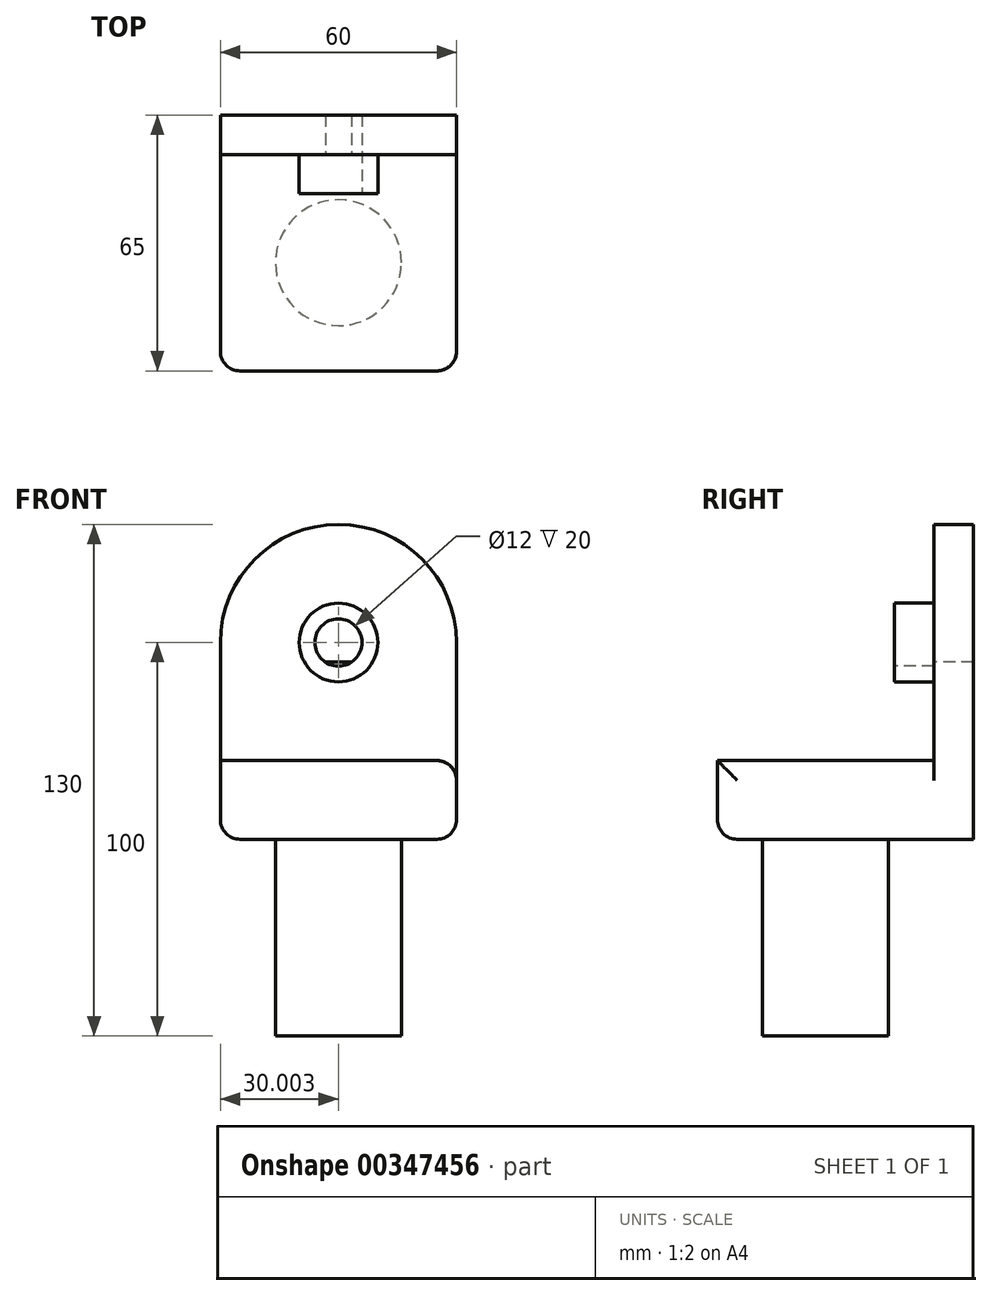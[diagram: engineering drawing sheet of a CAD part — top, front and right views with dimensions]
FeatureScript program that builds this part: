
annotation { "Feature Type Name" : "Feature", "Feature Type Description" : "" }
export const myFeature = defineFeature(function(context is Context, id is Id, definition is map)
    precondition{}
    {
        {
            var Q0;
            Q0=qCreatedBy(makeId("Top.planeOp"),FACE);
            var sketch = newSketch(context, id + "F0", { "sketchPlane" : qUnion([Q0])});
            skCircle(sketch, "E0", {"center": v(-36.32, -31.14) * mm, "radius": 16 * mm});
            skSolve(sketch);
        }
        {
            var Q0;
            Q0 = qSketchRegion(id + "F0", true);
            extrude(context, id + "F1", {"entities" : qUnion([Q0]), "depth" : 50 * mm});
        }
        {
            var Q0;
            Q0=makeQuery(id+"F1.opExtrude","CAP_FACE",FACE,{"disambiguationData":[OSD([sQuery(id+"F0.wireOp",EDGE,"E0")])],"isStart":false});
            var sketch = newSketch(context, id + "F2", { "sketchPlane" : qUnion([Q0])});
            skLineSegment(sketch, "E1", {"start": v(-66.32, -31.14) * mm, "end": v(-66.32, -3.64) * mm});
            skLineSegment(sketch, "E2", {"start": v(-66.32, -3.64) * mm, "end": v(-36.32, -3.64) * mm});
            skLineSegment(sketch, "E3", {"start": v(-66.32, -31.14) * mm, "end": v(-66.32, -58.64) * mm});
            skLineSegment(sketch, "E4", {"start": v(-66.32, -58.64) * mm, "end": v(-36.32, -58.64) * mm});
            skLineSegment(sketch, "E5", {"start": v(-36.32, -58.64) * mm, "end": v(-6.32, -58.64) * mm});
            skLineSegment(sketch, "E6", {"start": v(-6.32, -58.64) * mm, "end": v(-6.32, -31.14) * mm});
            skLineSegment(sketch, "E7", {"start": v(-36.32, -3.64) * mm, "end": v(-6.32, -3.64) * mm});
            skLineSegment(sketch, "E8", {"start": v(-6.32, -3.64) * mm, "end": v(-6.32, -31.14) * mm});
            skSolve(sketch);
        }
        {
            var Q0;
            Q0 = qSketchRegion(id + "F2", true);
            extrude(context, id + "F3", {"entities" : qUnion([Q0]), "operationType" : NewBodyOperationType.ADD, "depth" : 20 * mm});
        }
        {
            var Q0;
            Q0=makeQuery(id+"F3.opExtrude","CAP_FACE",FACE,{"disambiguationData":[OSD([sQuery(id+"F2.wireOp",EDGE,"E1"),sQuery(id+"F2.wireOp",EDGE,"E2"),sQuery(id+"F2.wireOp",EDGE,"E3"),sQuery(id+"F2.wireOp",EDGE,"E4"),sQuery(id+"F2.wireOp",EDGE,"E5"),sQuery(id+"F2.wireOp",EDGE,"E6"),sQuery(id+"F2.wireOp",EDGE,"E7"),sQuery(id+"F2.wireOp",EDGE,"E8")])],"isStart":false});
            var sketch = newSketch(context, id + "F4", { "sketchPlane" : qUnion([Q0])});
            skLineSegment(sketch, "E9", {"start": v(-66.32, -3.64) * mm, "end": v(-66.32, 6.36) * mm});
            skLineSegment(sketch, "E10", {"start": v(-6.32, -3.64) * mm, "end": v(-6.32, 6.36) * mm});
            skLineSegment(sketch, "E11", {"start": v(-6.32, 6.36) * mm, "end": v(-66.32, 6.36) * mm});
            skLineSegment(sketch, "E12", {"start": v(-66.32, -3.64) * mm, "end": v(-6.32, -3.64) * mm});
            skSolve(sketch);
        }
        {
            var Q0;
            Q0 = qSketchRegion(id + "F4", true);
            extrude(context, id + "F5", {"entities" : qUnion([Q0]), "operationType" : NewBodyOperationType.ADD, "oppositeDirection" : true, "depth" : 20 * mm});
        }
        {
            var Q0;
            Q0=makeQuery(id+"F5.boolean.opBoolean","MERGE",FACE,{"derivedFrom":[makeQuery(id+"F3.opExtrude","CAP_FACE",FACE,{"disambiguationData":[OSD([sQuery(id+"F2.wireOp",EDGE,"E1"),sQuery(id+"F2.wireOp",EDGE,"E2"),sQuery(id+"F2.wireOp",EDGE,"E3"),sQuery(id+"F2.wireOp",EDGE,"E4"),sQuery(id+"F2.wireOp",EDGE,"E5"),sQuery(id+"F2.wireOp",EDGE,"E6"),sQuery(id+"F2.wireOp",EDGE,"E7"),sQuery(id+"F2.wireOp",EDGE,"E8")])],"isStart":false}),makeQuery(id+"F5.opExtrude","CAP_FACE",FACE,{"disambiguationData":[OSD([sQuery(id+"F4.wireOp",EDGE,"E9"),sQuery(id+"F4.wireOp",EDGE,"E10"),sQuery(id+"F4.wireOp",EDGE,"E11"),sQuery(id+"F4.wireOp",EDGE,"E12")])],"isStart":true})]});
            var sketch = newSketch(context, id + "F6", { "sketchPlane" : qUnion([Q0])});
            skLineSegment(sketch, "E13", {"start": v(-66.32, -3.64) * mm, "end": v(-6.32, -3.64) * mm});
            skLineSegment(sketch, "E14", {"start": v(-6.32, -3.64) * mm, "end": v(-6.32, 6.36) * mm});
            skLineSegment(sketch, "E15", {"start": v(-6.32, 6.36) * mm, "end": v(-66.32, 6.36) * mm});
            skLineSegment(sketch, "E16", {"start": v(-66.32, 6.36) * mm, "end": v(-66.32, -3.64) * mm});
            skSolve(sketch);
        }
        {
            var Q0;
            Q0 = qSketchRegion(id + "F6", true);
            extrude(context, id + "F7", {"entities" : qUnion([Q0]), "operationType" : NewBodyOperationType.ADD, "depth" : 60 * mm});
        }
        {
            var Q0;
            Q0=makeQuery(id+"F7.opExtrude","CAP_EDGE",EDGE,{"disambiguationData":[OSD([sQuery(id+"F6.wireOp",EDGE,"E16")])],"isStart":false});
            var Q1;
            Q1=makeQuery(id+"F7.opExtrude","CAP_EDGE",EDGE,{"disambiguationData":[OSD([sQuery(id+"F6.wireOp",EDGE,"E14")])],"isStart":false});
            fillet(context, id + "F8", {"entities" : qUnion([Q0, Q1]), "radius" : 30 * mm, "tangentPropagation" : true, "allowEdgeOverflow" : false});
        }
        {
            var Q0;
            Q0=makeQuery(id+"F7.opExtrude","SWEPT_FACE",FACE,{"disambiguationData":[OSD([sQuery(id+"F6.wireOp",EDGE,"E13")])]});
            var sketch = newSketch(context, id + "F9", { "sketchPlane" : qUnion([Q0])});
            skLineSegment(sketch, "E17", {"start": v(-36.32, 130) * mm, "end": v(-36.32, 100) * mm, "construction": true});
            skCircle(sketch, "E18", {"center": v(-36.32, 100) * mm, "radius": 10 * mm});
            skSolve(sketch);
        }
        {
            var Q0;
            Q0 = qSketchRegion(id + "F9", true);
            extrude(context, id + "F10", {"entities" : qUnion([Q0]), "operationType" : NewBodyOperationType.ADD, "depth" : 10 * mm});
        }
        {
            var Q0;
            Q0=makeQuery(id+"F10.opExtrude","CAP_FACE",FACE,{"disambiguationData":[OSD([sQuery(id+"F9.wireOp",EDGE,"E18")])],"isStart":false});
            var sketch = newSketch(context, id + "F11", { "sketchPlane" : qUnion([Q0])});
            skCircle(sketch, "E19", {"center": v(-36.32, 100) * mm, "radius": 6 * mm});
            skSolve(sketch);
        }
        {
            var Q0;
            Q0 = qSketchRegion(id + "F11", true);
            extrude(context, id + "F12", {"entities" : qUnion([Q0]), "operationType" : NewBodyOperationType.REMOVE, "endBound" : BoundingType.THROUGH_ALL, "oppositeDirection" : true, "depth" : 25 * mm});
        }
        {
            var Q0;
            Q0=makeQuery(id+"F5.boolean.opBoolean","MERGE",FACE,{"derivedFrom":[makeQuery(id+"F3.opExtrude","CAP_FACE",FACE,{"disambiguationData":[OSD([sQuery(id+"F2.wireOp",EDGE,"E1"),sQuery(id+"F2.wireOp",EDGE,"E2"),sQuery(id+"F2.wireOp",EDGE,"E3"),sQuery(id+"F2.wireOp",EDGE,"E4"),sQuery(id+"F2.wireOp",EDGE,"E5"),sQuery(id+"F2.wireOp",EDGE,"E6"),sQuery(id+"F2.wireOp",EDGE,"E7"),sQuery(id+"F2.wireOp",EDGE,"E8")])],"isStart":false}),makeQuery(id+"F5.opExtrude","CAP_FACE",FACE,{"disambiguationData":[OSD([sQuery(id+"F4.wireOp",EDGE,"E9"),sQuery(id+"F4.wireOp",EDGE,"E10"),sQuery(id+"F4.wireOp",EDGE,"E11"),sQuery(id+"F4.wireOp",EDGE,"E12")])],"isStart":true})]});
            var sketch = newSketch(context, id + "F13", { "sketchPlane" : qUnion([Q0])});
            skSolve(sketch);
        }
        {
            var Q0;
            Q0=makeQuery(id+"F3.opExtrude","SWEPT_EDGE",EDGE,{"disambiguationData":[OSD([sQuery(id+"F2.wireOp",EDGE,"E3"),sQuery(id+"F2.wireOp",EDGE,"E4")])]});
            var Q1;
            Q1=makeQuery(id+"F5.boolean.opBoolean","MERGE",EDGE,{"derivedFrom":[makeQuery(id+"F3.opExtrude","CAP_EDGE",EDGE,{"disambiguationData":[OSD([sQuery(id+"F2.wireOp",EDGE,"E1"),sQuery(id+"F2.wireOp",EDGE,"E3")])],"isStart":true}),makeQuery(id+"F5.opExtrude","CAP_EDGE",EDGE,{"disambiguationData":[OSD([sQuery(id+"F4.wireOp",EDGE,"E9")])],"isStart":false})]});
            var Q2;
            Q2=makeQuery(id+"F3.opExtrude","CAP_EDGE",EDGE,{"disambiguationData":[OSD([sQuery(id+"F2.wireOp",EDGE,"E4"),sQuery(id+"F2.wireOp",EDGE,"E5")])],"isStart":true});
            var Q3;
            Q3=makeQuery(id+"F5.boolean.opBoolean","MERGE",EDGE,{"derivedFrom":[makeQuery(id+"F3.opExtrude","CAP_EDGE",EDGE,{"disambiguationData":[OSD([sQuery(id+"F2.wireOp",EDGE,"E6"),sQuery(id+"F2.wireOp",EDGE,"E8")])],"isStart":true}),makeQuery(id+"F5.opExtrude","CAP_EDGE",EDGE,{"disambiguationData":[OSD([sQuery(id+"F4.wireOp",EDGE,"E10")])],"isStart":false})]});
            var Q4;
            Q4=makeQuery(id+"F3.opExtrude","SWEPT_EDGE",EDGE,{"disambiguationData":[OSD([sQuery(id+"F2.wireOp",EDGE,"E5"),sQuery(id+"F2.wireOp",EDGE,"E6")])]});
            var Q5;
            Q5=makeQuery(id+"F5.boolean.opBoolean","MERGE",EDGE,{"derivedFrom":[makeQuery(id+"F3.opExtrude","CAP_EDGE",EDGE,{"disambiguationData":[OSD([sQuery(id+"F2.wireOp",EDGE,"E6"),sQuery(id+"F2.wireOp",EDGE,"E8")])],"isStart":false}),makeQuery(id+"F5.opExtrude","CAP_EDGE",EDGE,{"disambiguationData":[OSD([sQuery(id+"F4.wireOp",EDGE,"E10")])],"isStart":true})]});
            fillet(context, id + "F14", {"entities" : qUnion([Q0, Q1, Q2, Q3, Q4, Q5]), "radius" : 5 * mm, "tangentPropagation" : true, "allowEdgeOverflow" : false});
        }
        {
            var Q0;
            Q0 = qSketchRegion(id + "F6", true);
            extrude(context, id + "F15", {"entities" : qUnion([Q0]), "operationType" : NewBodyOperationType.ADD, "depth" : 25 * mm});
        }
    });
